# Revit family: WashbasinUnit-100cm-WithTwoDrawer-Vitra-NestTrendySeries-56442+56149+56150+56151
name_source: partatom
category: Furniture Systems
revit_build: Autodesk Revit 2017 (Build: 20160225_1515(x64)
units: mm (PartAtom-declared; Revit-internal decimal feet)

## family parameters
Cut with Voids When Loaded = No
Host = Face
OmniClass Number = 23.40.00.00
OmniClass Title = Equipment and Furnishings
Part Type = Normal
Room Calculation Point = No
Round Connector Dimension = Use Diameter
Shared = Yes

## types (4) — shared parameters
BIMobject category = Bathroom compound units
Brand = VitrA
Default Elevation = 660 mm
Description = Nest Trendy Washbasin Unit 100cm - with two Drawer
Design country = Turkey
IFC Classification = Furniture
Main Material = Wood
Manufacturer = VitrA
Manufacturer name = VitrA
Masterformat 2014 Code = 13 42 13
Masterformat 2014 Description = Bathroom Unit Modules
Mounting type = Wall Hung
NBS Referans Code = 35-75-08
NBS Referans Description = Bathroom Cabinets
Nominal Depth (mm) = 435 mm
Nominal Height (mm) = 520 mm
Nominal Width (mm) = 965 mm
OmniClass Code = 23-31 25 13
OmniClass Description = Bathroom Cabinets
Product certification = https://www.vitraglobal.com
Product family = Nest Trendy
Product group = Washbasin Unit - with two Drawer
Product url = https://www.vitra.com.tr
Secondary Material = Metal
Technical description = https://www.vitra.com.tr
UNSPSC Code = 301815
UNSPSC Description = Bathroom Cabinets
URL = https://vitraglobal.com
Uniclass 1.4 Code = L8241
Uniclass 1.4 Description = Bathroom Cabinets
Uniclass 2.0 Code = PR-35-75-08
Uniclass 2.0 Description = Bathroom Cabinets
Uniclass 2015 Code = Pr_40_20_93
Uniclass 2015 Name = Wash basins, sinks and troughs
Uniformat II Code = E20
Uniformat II Description = FURNISHINGS
Warranty Period (Year) = 2
Youtube = https://www.youtube.com

## per-type parameters (varying)
| type | Article No. (default) | Color | Model | Primary Material | Product SKU | Product data url |
| WashbasinUnit-100cm-WithTwoDrawer-Vitra-NestTrendySeries-56442 | 56442 | Brilliant White | 56442 | Brilliant White | 56442 | https://www.bimobject.com |
| WashbasinUnit-100cm-WithTwoDrawer-Vitra-NestTrendySeries-56149 | 56149 | High Gloss Anthracite | 56149 | High Gloss Anthracite | 56149 |  |
| WashbasinUnit-100cm-WithTwoDrawer-Vitra-NestTrendySeries-56150 | 56150 | Waved Natural Wood | 56150 | Waved Natural Wood | 56150 |  |
| WashbasinUnit-100cm-WithTwoDrawer-Vitra-NestTrendySeries-56151 | 56151 | Grey Natural Wood | 56151 | Grey Natural Wood | 56151 |  |

## geometry (parser evidence)
native form markers: Sweep x2
no freeform markers — native parametric forms only
